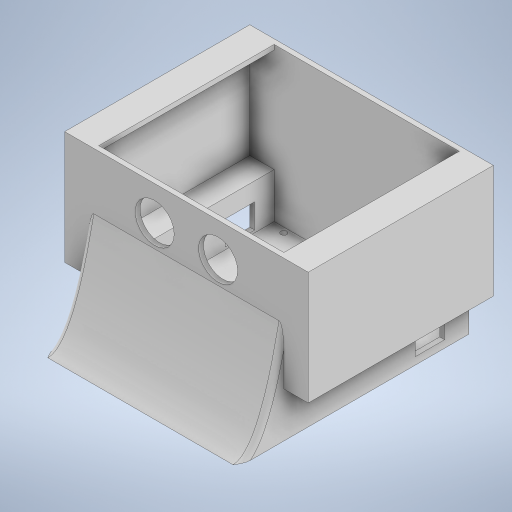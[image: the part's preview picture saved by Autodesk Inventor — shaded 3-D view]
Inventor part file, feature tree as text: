
AUTODESK INVENTOR PART (.ipt)
format: ipt  version: 2024 (Build 280153000, 153)  size: 373,760 bytes
history: native  units: mm
features: sketch x10, extrude x9, shell x2, fillet x1
ambient origin geometry x8: Origin, YZ Plane, XZ Plane, XY Plane, X Axis, Y Axis, Z Axis, Center Point
bodies: Solid1 (feature_tree)
feature tree (22):
  sketch  "Sketch2"  dims[d0=38.0mm d1=38.0mm d2=40.0mm]
  extrude  "Extrusion1"  Depth=38.0mm
  shell  "Shell1"  Thickness=40.0mm
  sketch  "Sketch8"  dims[d6=2.0mm d18=10.05mm]
  extrude  "Extrusion4"  Depth=65.0mm TaperAngle=0.0deg
  extrude  "Extrusion5"  Depth=2.0mm
  extrude  "Extrusion6"  Depth=90.0mm
  shell  "Shell2"  Thickness=90.0mm
  extrude  "Extrusion7"  Depth=10.0mm TaperAngle=0.0deg
  fillet  "Fillet2"  Radius=10.0mm
  extrude  "Extrusion8"  Depth=6.0mm
  extrude  "Extrusion9"  Depth=80.0mm TaperAngle=0.0deg
  sketch  "Sketch16"  dims[d40=16.05mm d41=26.05mm]
  extrude  "Extrusion10"  Depth=2.0mm
  extrude  "Extrusion11"  Depth=26.05mm
  sketch  "Sketch3"  dims[d3=40.0mm d4=65.0mm d5=0.0mm]
  sketch  "Sketch10"  dims[d19=12.05mm d20=13.05mm d26=90.0mm d27=0.0mm]
  sketch  "Sketch11"  dims[d28=46.5mm d29=10.0mm d30=0.0mm d31=10.0mm d32=0.0mm]
  sketch  "Sketch12"  dims[d33=2.0mm d34=6.0mm]
  sketch  "Sketch13"  dims[d35=13.0mm d36=80.0mm d37=0.0mm]
  sketch  "Sketch15"  dims[d38=2.0mm d39=16.05mm]
  sketch  "Sketch17"  dims[d42=2.0mm d43=0.0mm d44=10.0mm d45=18.0mm d46=18.0mm d47=8.0mm d49=8.0mm d50=8.0mm d51=8.0mm d52=4.0mm d53=4.0mm d54=2.5mm d55=2.5mm d56=2.5mm d57=2.5mm d58=10.0mm d59=0.0mm d60=2.0mm d61=4.0mm d62=16.0mm d63=4.0mm d64=16.0mm d65=2.0mm d66=8.0mm d67=10.0mm d68=0.0mm d69=10.0mm d70=0.0mm d72=14.0mm d73=14.0mm d74=37.0mm d75=10.0mm]
